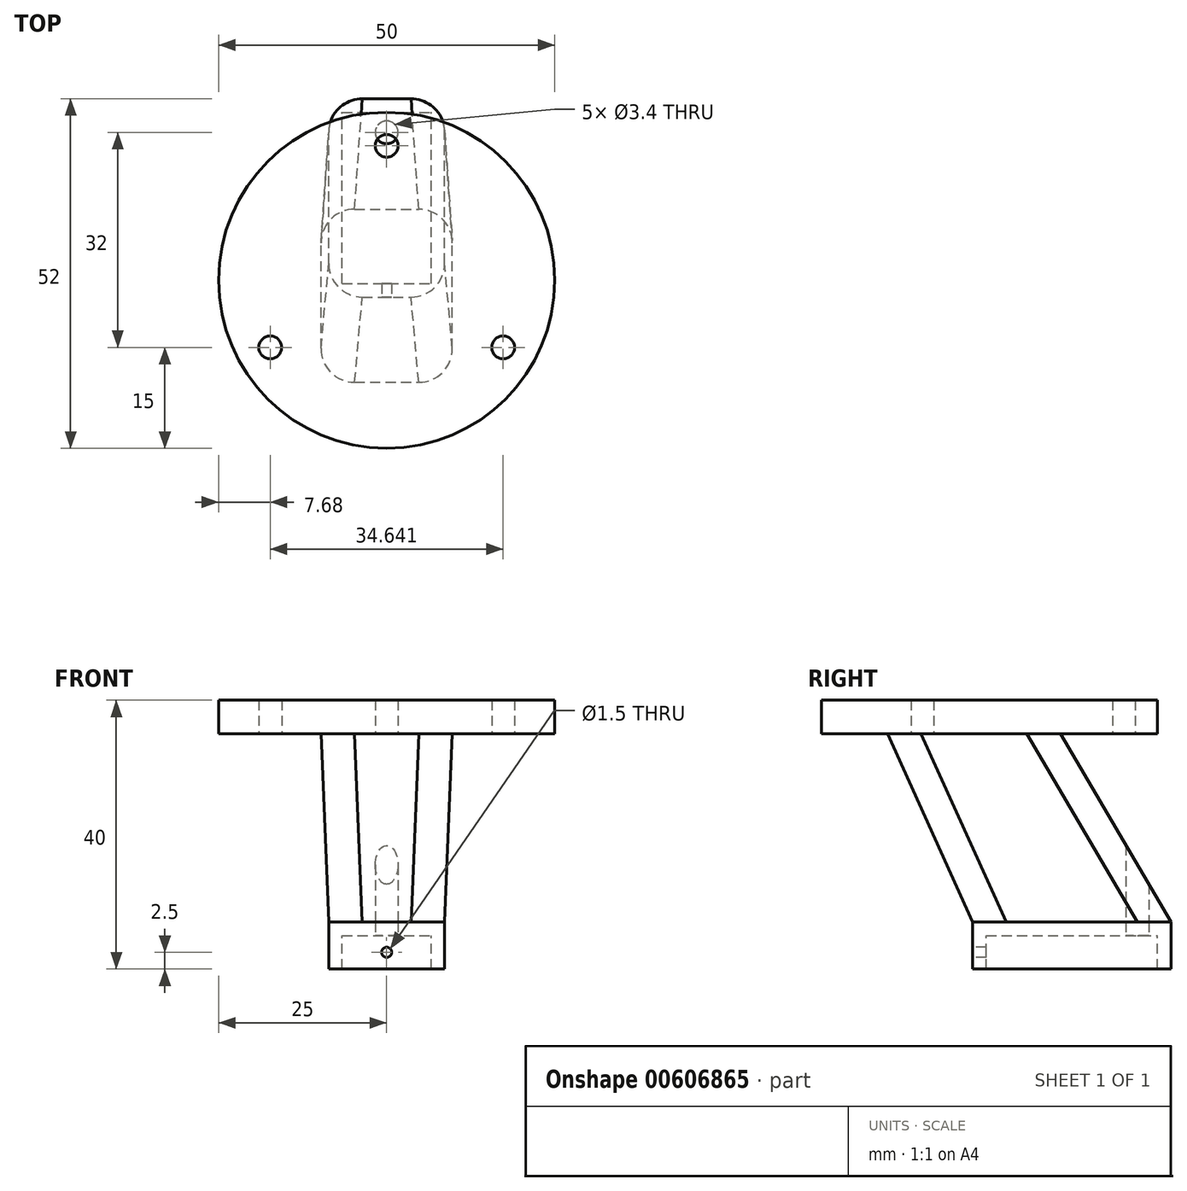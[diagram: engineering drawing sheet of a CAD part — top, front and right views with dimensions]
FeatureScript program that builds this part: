
annotation { "Feature Type Name" : "Feature", "Feature Type Description" : "" }
export const myFeature = defineFeature(function(context is Context, id is Id, definition is map)
    precondition{}
    {
        {
            var Q0;
            Q0=qCreatedBy(makeId("Top.planeOp"),FACE);
            var sketch = newSketch(context, id + "F0", { "sketchPlane" : qUnion([Q0])});
            skPoint(sketch, "E0.0", {"position": v(0, 0) * mm});
            skCircle(sketch, "E1", {"center": v(0, 0) * mm, "radius": 25 * mm});
            skCircle(sketch, "E2", {"center": v(0, 20) * mm, "radius": 1.7 * mm});
            skCircle(sketch, "E3", {"center": v(0, 0) * mm, "radius": 20 * mm, "construction": true});
            skCircle(sketch, "E4.1.0", {"center": v(-17.32, -10) * mm, "radius": 1.7 * mm});
            skCircle(sketch, "E4.2.0", {"center": v(17.32, -10) * mm, "radius": 1.7 * mm});
            skSolve(sketch);
        }
        {
            var Q0;
            Q0=makeQuery(id+"F0.imprint","IMPRINT",FACE,{"disambiguationData":[TD([[makeQuery(id+"F0.imprint","IMPRINT",EDGE,{"derivedFrom":sQuery(id+"F0.wireOp",EDGE,"E1")}),1.0]])]});
            extrude(context, id + "F1", {"entities" : qUnion([Q0]), "depth" : 5 * mm, "offsetDistance" : 25 * mm});
        }
        {
            var Q0;
            Q0=qCreatedBy(makeId("Top.planeOp"),FACE);
            cPlane(context, id + "F2", {"entities" : qUnion([Q0]), "cplaneType" : CPlaneType.OFFSET, "offset" : 30 * mm, "oppositeDirection" : true, "width" : 150 * mm, "height" : 150 * mm});
        }
        {
            var Q0;
            Q0=qCreatedBy(id+"F2.planeOp",FACE);
            var sketch = newSketch(context, id + "F3", { "sketchPlane" : qUnion([Q0])});
            skLineSegment(sketch, "E5.bottom", {"start": v(-6.12, 0) * mm, "end": v(6.12, 0) * mm, "construction": true});
            skLineSegment(sketch, "E5.top", {"start": v(-6.13, 24.5) * mm, "end": v(6.13, 24.5) * mm, "construction": true});
            skLineSegment(sketch, "E5.left", {"start": v(-6.12, 0) * mm, "end": v(-6.12, 24.5) * mm, "construction": true});
            skLineSegment(sketch, "E5.right", {"start": v(6.12, 0) * mm, "end": v(6.12, 24.5) * mm, "construction": true});
            skPoint(sketch, "E6", {"position": v(0, 0) * mm});
            skLineSegment(sketch, "E7.0", {"start": v(-8.62, -2.5) * mm, "end": v(-8.63, 27) * mm});
            skLineSegment(sketch, "E7.1", {"start": v(-8.62, -2.5) * mm, "end": v(8.62, -2.5) * mm});
            skLineSegment(sketch, "E7.2", {"start": v(8.62, -2.5) * mm, "end": v(8.62, 27) * mm});
            skLineSegment(sketch, "E7.3", {"start": v(-8.62, 27) * mm, "end": v(8.62, 27) * mm});
            skLineSegment(sketch, "E8.0", {"start": v(-6.62, -0.5) * mm, "end": v(6.62, -0.5) * mm});
            skLineSegment(sketch, "E8.1", {"start": v(-6.62, -0.5) * mm, "end": v(-6.63, 25) * mm});
            skLineSegment(sketch, "E8.2", {"start": v(-6.63, 25) * mm, "end": v(6.63, 25) * mm});
            skLineSegment(sketch, "E8.3", {"start": v(6.63, -0.5) * mm, "end": v(6.62, 25) * mm});
            skCircle(sketch, "E9", {"center": v(0, 22) * mm, "radius": 1.7 * mm});
            skPoint(sketch, "E9.centerSnap0", {"position": v(0, 24.5) * mm});
            skSolve(sketch);
        }
        {
            var Q0;
            Q0=makeQuery(id+"F3.imprint","IMPRINT",FACE,{"disambiguationData":[TD([[makeQuery(id+"F3.imprint","IMPRINT",EDGE,{"derivedFrom":sQuery(id+"F3.wireOp",EDGE,"E7.0")}),-1.0]])]});
            extrude(context, id + "F4", {"entities" : qUnion([Q0]), "oppositeDirection" : true, "depth" : 5 * mm, "offsetDistance" : 25 * mm});
        }
        {
            var Q0;
            Q0=makeQuery(id+"F3.imprint","IMPRINT",FACE,{"disambiguationData":[TD([[makeQuery(id+"F3.imprint","IMPRINT",EDGE,{"derivedFrom":sQuery(id+"F3.wireOp",EDGE,"E7.0")}),-1.0]])]});
            var Q1;
            Q1=makeQuery(id+"F3.imprint","IMPRINT",FACE,{"disambiguationData":[TD([[makeQuery(id+"F3.imprint","IMPRINT",EDGE,{"derivedFrom":sQuery(id+"F3.wireOp",EDGE,"E8.0")}),1.0]])]});
            var Q2;
            Q2=makeQuery(id+"F3.imprint","IMPRINT",FACE,{"disambiguationData":[TD([[makeQuery(id+"F3.imprint","IMPRINT",EDGE,{"derivedFrom":sQuery(id+"F3.wireOp",EDGE,"E9")}),1.0]])]});
            extrude(context, id + "F5", {"entities" : qUnion([Q0, Q1, Q2]), "operationType" : NewBodyOperationType.ADD, "depth" : 2 * mm, "offsetDistance" : 25 * mm});
        }
        {
            var Q0;
            {var subQ0=sQuery(id+"F3.wireOp",EDGE,"E7.1");Q0=makeQuery(id+"F5.boolean.opBoolean","MERGE",FACE,{"derivedFrom":[makeQuery(id+"F4.opExtrude","SWEPT_FACE",FACE,{"disambiguationData":[OSD([subQ0])]}),makeQuery(id+"F5.opExtrude","SWEPT_FACE",FACE,{"disambiguationData":[OSD([subQ0])]})]});}
            var sketch = newSketch(context, id + "F6", { "sketchPlane" : qUnion([Q0])});
            skCircle(sketch, "E10", {"center": v(0, -32.5) * mm, "radius": 0.75 * mm});
            skLineSegment(sketch, "E11.0", {"start": v(-8.62, -30) * mm, "end": v(8.62, -30) * mm, "construction": true});
            skLineSegment(sketch, "E12", {"start": v(8.62, -30) * mm, "end": v(8.62, -35) * mm, "construction": true});
            skPoint(sketch, "E13", {"position": v(8.62, -32.5) * mm});
            skSolve(sketch);
        }
        {
            var Q0;
            Q0=makeQuery(id+"F6.imprint","IMPRINT",FACE,{"disambiguationData":[TD([[makeQuery(id+"F6.imprint","IMPRINT",EDGE,{"derivedFrom":sQuery(id+"F6.wireOp",EDGE,"E10")}),1.0]])]});
            extrude(context, id + "F7", {"entities" : qUnion([Q0]), "operationType" : NewBodyOperationType.REMOVE, "endBound" : BoundingType.UP_TO_NEXT, "oppositeDirection" : true, "depth" : 25 * mm, "offsetDistance" : 25 * mm});
        }
        {
            var Q0;
            {var subQ0=sQuery(id+"F3.wireOp",EDGE,"E7.2");var subQ1=sQuery(id+"F3.wireOp",EDGE,"E7.1");Q0=makeQuery(id+"F5.boolean.opBoolean","MERGE",EDGE,{"derivedFrom":[makeQuery(id+"F4.opExtrude","SWEPT_EDGE",EDGE,{"disambiguationData":[OSD([subQ1,subQ0])]}),makeQuery(id+"F5.opExtrude","SWEPT_EDGE",EDGE,{"disambiguationData":[OSD([subQ1,subQ0])]})]});}
            var Q1;
            {var subQ0=sQuery(id+"F3.wireOp",EDGE,"E7.3");var subQ1=sQuery(id+"F3.wireOp",EDGE,"E7.2");Q1=makeQuery(id+"F5.boolean.opBoolean","MERGE",EDGE,{"derivedFrom":[makeQuery(id+"F4.opExtrude","SWEPT_EDGE",EDGE,{"disambiguationData":[OSD([subQ1,subQ0])]}),makeQuery(id+"F5.opExtrude","SWEPT_EDGE",EDGE,{"disambiguationData":[OSD([subQ1,subQ0])]})]});}
            var Q2;
            {var subQ0=sQuery(id+"F3.wireOp",EDGE,"E7.1");var subQ1=sQuery(id+"F3.wireOp",EDGE,"E7.0");Q2=makeQuery(id+"F5.boolean.opBoolean","MERGE",EDGE,{"derivedFrom":[makeQuery(id+"F4.opExtrude","SWEPT_EDGE",EDGE,{"disambiguationData":[OSD([subQ1,subQ0])]}),makeQuery(id+"F5.opExtrude","SWEPT_EDGE",EDGE,{"disambiguationData":[OSD([subQ1,subQ0])]})]});}
            var Q3;
            {var subQ0=sQuery(id+"F3.wireOp",EDGE,"E7.3");var subQ1=sQuery(id+"F3.wireOp",EDGE,"E7.0");Q3=makeQuery(id+"F5.boolean.opBoolean","MERGE",EDGE,{"derivedFrom":[makeQuery(id+"F4.opExtrude","SWEPT_EDGE",EDGE,{"disambiguationData":[OSD([subQ1,subQ0])]}),makeQuery(id+"F5.opExtrude","SWEPT_EDGE",EDGE,{"disambiguationData":[OSD([subQ1,subQ0])]})]});}
            fillet(context, id + "F8", {"entities" : qUnion([Q0, Q1, Q2, Q3]), "radius" : 5 * mm, "tangentPropagation" : true, "allowEdgeOverflow" : false});
        }
        {
            var Q0;
            Q0=makeQuery(id+"F1.opExtrude","CAP_FACE",FACE,{"disambiguationData":[OSD([sQuery(id+"F0.wireOp",EDGE,"E1"),sQuery(id+"F0.wireOp",EDGE,"E2"),sQuery(id+"F0.wireOp",EDGE,"E4.1.0"),sQuery(id+"F0.wireOp",EDGE,"E4.2.0")])],"isStart":true});
            var sketch = newSketch(context, id + "F9", { "sketchPlane" : qUnion([Q0])});
            skLineSegment(sketch, "E14.bottom", {"start": v(-4.77, 15.18) * mm, "end": v(4.77, 15.18) * mm});
            skLineSegment(sketch, "E14.top", {"start": v(-4.77, -10.56) * mm, "end": v(4.77, -10.56) * mm});
            skLineSegment(sketch, "E14.left", {"start": v(-9.77, 10.18) * mm, "end": v(-9.77, -5.56) * mm});
            skLineSegment(sketch, "E14.right", {"start": v(9.77, 10.18) * mm, "end": v(9.77, -5.56) * mm});
            skPoint(sketch, "E15", {"position": v(0, 15.18) * mm});
            skPoint(sketch, "E16.visualSharp", {"position": v(-9.77, 15.18) * mm});
            skArc(sketch, "E16.filletArc", {"start": v(-4.77, 15.18) * mm, "mid": v(-8.3, 13.71) * mm, "end": v(-9.77, 10.18) * mm});
            skPoint(sketch, "E17.visualSharp", {"position": v(9.77, 15.18) * mm});
            skArc(sketch, "E17.filletArc", {"start": v(9.77, 10.18) * mm, "mid": v(8.3, 13.71) * mm, "end": v(4.77, 15.18) * mm});
            skPoint(sketch, "E18.visualSharp", {"position": v(9.77, -10.56) * mm});
            skArc(sketch, "E18.filletArc", {"start": v(4.77, -10.56) * mm, "mid": v(8.3, -9.1) * mm, "end": v(9.77, -5.56) * mm});
            skPoint(sketch, "E19.visualSharp", {"position": v(-9.77, -10.56) * mm});
            skArc(sketch, "E19.filletArc", {"start": v(-9.77, -5.56) * mm, "mid": v(-8.3, -9.1) * mm, "end": v(-4.77, -10.56) * mm});
            skSolve(sketch);
        }
        {
            var Q0;
            Q0=makeQuery(id+"F5.opExtrude","CAP_FACE",FACE,{"disambiguationData":[OSD([sQuery(id+"F3.wireOp",EDGE,"E7.0"),sQuery(id+"F3.wireOp",EDGE,"E7.1"),sQuery(id+"F3.wireOp",EDGE,"E7.2"),sQuery(id+"F3.wireOp",EDGE,"E7.3"),sQuery(id+"F3.wireOp",EDGE,"E9")])],"isStart":false});
            var sketch = newSketch(context, id + "F10", { "sketchPlane" : qUnion([Q0])});
            skLineSegment(sketch, "E20.0", {"start": v(-3.62, -2.5) * mm, "end": v(3.63, -2.5) * mm});
            skArc(sketch, "E21.0", {"start": v(3.62, -2.5) * mm, "mid": v(7.16, -1.04) * mm, "end": v(8.62, 2.5) * mm});
            skLineSegment(sketch, "E22.0", {"start": v(8.62, 2.5) * mm, "end": v(8.62, 22) * mm});
            skArc(sketch, "E23.0", {"start": v(8.62, 22) * mm, "mid": v(7.16, 25.54) * mm, "end": v(3.62, 27) * mm});
            skLineSegment(sketch, "E24.0", {"start": v(-3.63, 27) * mm, "end": v(3.62, 27) * mm});
            skArc(sketch, "E25.0", {"start": v(-3.62, 27) * mm, "mid": v(-7.16, 25.54) * mm, "end": v(-8.62, 22) * mm});
            skLineSegment(sketch, "E26.0", {"start": v(-8.62, 2.5) * mm, "end": v(-8.62, 22) * mm});
            skPoint(sketch, "E27.0", {"position": v(-7.16, -1.04) * mm});
            skArc(sketch, "E28.0", {"start": v(-8.62, 2.5) * mm, "mid": v(-7.16, -1.04) * mm, "end": v(-3.62, -2.5) * mm});
            skSolve(sketch);
        }
        {
            var Q0;
            Q0=makeQuery(id+"F9.imprint","IMPRINT",FACE,{"disambiguationData":[TD([[makeQuery(id+"F9.imprint","IMPRINT",EDGE,{"derivedFrom":sQuery(id+"F9.wireOp",EDGE,"E14.bottom")}),-1.0]])]});
            var Q1;
            Q1=makeQuery(id+"F10.imprint","IMPRINT",FACE,{"disambiguationData":[TD([[makeQuery(id+"F10.imprint","IMPRINT",EDGE,{"derivedFrom":sQuery(id+"F10.wireOp",EDGE,"E20.0")}),1.0]])]});
            loft(context, id + "F11", {"sheetProfilesArray" : [{ "sheetProfileEntities" : qUnion([Q0]) }, { "sheetProfileEntities" : qUnion([Q1]) }]});
        }
        {
            var Q0;
            Q0=makeQuery(id+"F3.imprint","IMPRINT",FACE,{"disambiguationData":[TD([[makeQuery(id+"F3.imprint","IMPRINT",EDGE,{"derivedFrom":sQuery(id+"F3.wireOp",EDGE,"E9")}),1.0]])]});
            var Q1;
            Q1=makeQuery(id+"F11.opLoft","SWEPT_FACE",FACE,{"disambiguationData":[OSD([sQuery(id+"F9.wireOp",EDGE,"E14.top"),sQuery(id+"F9.wireOp",EDGE,"E18.filletArc"),sQuery(id+"F9.wireOp",EDGE,"E19.filletArc"),sQuery(id+"F10.wireOp",EDGE,"E23.0"),sQuery(id+"F10.wireOp",EDGE,"E24.0"),sQuery(id+"F10.wireOp",EDGE,"E25.0")])]});
            extrude(context, id + "F12", {"entities" : qUnion([Q0]), "operationType" : NewBodyOperationType.REMOVE, "depth" : 25 * mm, "endBoundEntityFace" : qUnion([Q1]), "offsetDistance" : 25 * mm});
        }
    });
